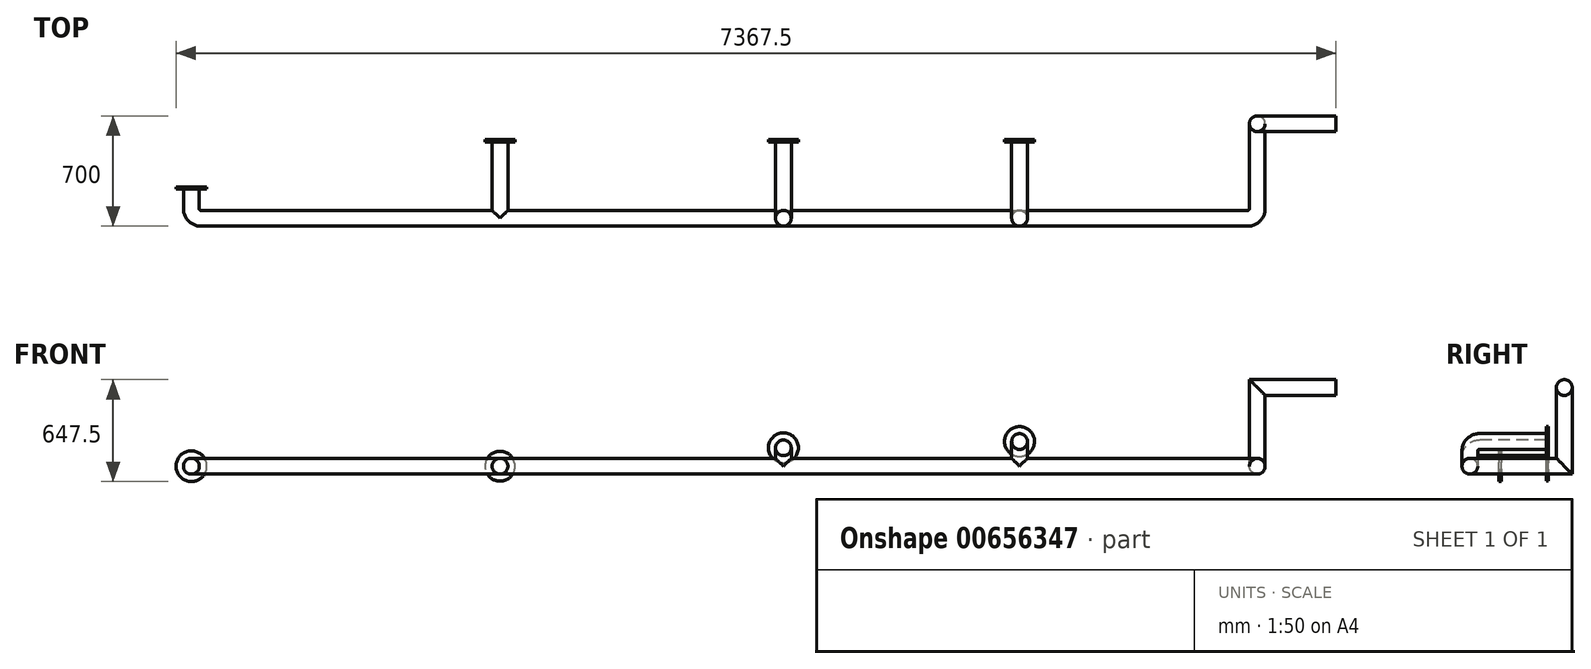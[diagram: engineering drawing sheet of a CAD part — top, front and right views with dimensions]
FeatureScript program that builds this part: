
annotation { "Feature Type Name" : "Feature", "Feature Type Description" : "" }
export const myFeature = defineFeature(function(context is Context, id is Id, definition is map)
    precondition{}
    {
        {
            var Q0;
            Q0=qCreatedBy(makeId("Top.planeOp"),FACE);
            var sketch = newSketch(context, id + "F0", { "sketchPlane" : qUnion([Q0])});
            skLineSegment(sketch, "E0", {"start": v(60, 0) * mm, "end": v(6710, 0) * mm});
            skLineSegment(sketch, "E1", {"start": v(6770, 60) * mm, "end": v(6770, 540) * mm});
            skLineSegment(sketch, "E2", {"start": v(0, 60) * mm, "end": v(0, 200) * mm});
            skLineSegment(sketch, "E3", {"start": v(1960.38, 0) * mm, "end": v(1960.38, 500) * mm});
            skLineSegment(sketch, "E4", {"start": v(3760, 0) * mm, "end": v(3760, 500) * mm});
            skLineSegment(sketch, "E5", {"start": v(5260, 0) * mm, "end": v(5260, 500) * mm});
            skPoint(sketch, "E6.visualSharp", {"position": v(0, 0) * mm});
            skArc(sketch, "E6.filletArc", {"start": v(0, 60) * mm, "mid": v(17.57, 17.57) * mm, "end": v(60, 0) * mm});
            skPoint(sketch, "E7.visualSharp", {"position": v(6770, 0) * mm});
            skArc(sketch, "E7.filletArc", {"start": v(6710, 0) * mm, "mid": v(6752.43, 17.57) * mm, "end": v(6770, 60) * mm});
            skPoint(sketch, "E8.visualSharp", {"position": v(6770, 600) * mm});
            skLineSegment(sketch, "E9", {"start": v(6770, 600) * mm, "end": v(6770, 540) * mm});
            skSolve(sketch);
        }
        {
            var Q0;
            Q0=qCreatedBy(makeId("Front.planeOp"),FACE);
            cPlane(context, id + "F1", {"entities" : qUnion([Q0]), "cplaneType" : CPlaneType.OFFSET, "offset" : 200 * mm, "oppositeDirection" : true, "width" : 150 * mm, "height" : 150 * mm});
        }
        {
            var Q0;
            Q0=qCreatedBy(id+"F1.planeOp",FACE);
            var sketch = newSketch(context, id + "F2", { "sketchPlane" : qUnion([Q0])});
            skCircle(sketch, "E10", {"center": v(0, 0) * mm, "radius": 97.5 * mm});
            skCircle(sketch, "E11", {"center": v(0, 0) * mm, "radius": 50 * mm});
            skSolve(sketch);
        }
        {
            var Q0;
            Q0=qCreatedBy(makeId("Front.planeOp"),FACE);
            cPlane(context, id + "F3", {"entities" : qUnion([Q0]), "cplaneType" : CPlaneType.OFFSET, "offset" : 500 * mm, "oppositeDirection" : true, "width" : 150 * mm, "height" : 150 * mm});
        }
        {
            var Q0;
            Q0=qCreatedBy(makeId("Right.planeOp"),FACE);
            cPlane(context, id + "F4", {"entities" : qUnion([Q0]), "cplaneType" : CPlaneType.OFFSET, "offset" : 6770 * mm, "width" : 150 * mm, "height" : 150 * mm});
        }
        {
            var Q0;
            Q0=qCreatedBy(id+"F4.planeOp",FACE);
            var sketch = newSketch(context, id + "F5", { "sketchPlane" : qUnion([Q0])});
            skPoint(sketch, "E12.0", {"position": v(600, 0) * mm});
            skLineSegment(sketch, "E13", {"start": v(600, 0) * mm, "end": v(600, 500) * mm});
            skSolve(sketch);
        }
        {
            var Q0;
            Q0=qCreatedBy(makeId("Front.planeOp"),FACE);
            cPlane(context, id + "F6", {"entities" : qUnion([Q0]), "cplaneType" : CPlaneType.OFFSET, "offset" : 600 * mm, "oppositeDirection" : true, "width" : 150 * mm, "height" : 150 * mm});
        }
        {
            var Q0;
            Q0=qCreatedBy(id+"F6.planeOp",FACE);
            var sketch = newSketch(context, id + "F7", { "sketchPlane" : qUnion([Q0])});
            skPoint(sketch, "E14.0", {"position": v(6770, 500) * mm});
            skLineSegment(sketch, "E15", {"start": v(6770, 500) * mm, "end": v(7270, 500) * mm});
            skSolve(sketch);
        }
        {
            var Q0;
            Q0=makeQuery(id+"F2.imprint","IMPRINT",FACE,{"disambiguationData":[TD([[makeQuery(id+"F2.imprint","IMPRINT",EDGE,{"derivedFrom":sQuery(id+"F2.wireOp",EDGE,"E11")}),1.0]])]});
            var Q1;
            Q1=sQuery(id+"F0.wireOp",EDGE,"E2");
            var Q2;
            Q2=sQuery(id+"F0.wireOp",EDGE,"E6.filletArc");
            var Q3;
            Q3=sQuery(id+"F0.wireOp",EDGE,"E0");
            var Q4;
            Q4=sQuery(id+"F0.wireOp",EDGE,"E7.filletArc");
            var Q5;
            Q5=sQuery(id+"F0.wireOp",EDGE,"E1");
            var Q6;
            Q6=sQuery(id+"F0.wireOp",EDGE,"E9");
            var Q7;
            Q7=sQuery(id+"F5.wireOp",EDGE,"E13");
            var Q8;
            Q8=sQuery(id+"F7.wireOp",EDGE,"E15");
            sweep(context, id + "F8", {"profiles" : qUnion([Q0]), "path" : qUnion([Q1, Q2, Q3, Q4, Q5, Q6, Q7, Q8])});
        }
        {
            var Q0;
            Q0=makeQuery(id+"F2.imprint","IMPRINT",FACE,{"disambiguationData":[TD([[makeQuery(id+"F2.imprint","IMPRINT",EDGE,{"derivedFrom":sQuery(id+"F2.wireOp",EDGE,"E10")}),1.0]])]});
            var Q1;
            Q1=makeQuery(id+"F2.imprint","IMPRINT",FACE,{"disambiguationData":[TD([[makeQuery(id+"F2.imprint","IMPRINT",EDGE,{"derivedFrom":sQuery(id+"F2.wireOp",EDGE,"E11")}),1.0]])]});
            var Q2;
            Q2=makeQuery(id+"F14.imprint","IMPRINT",FACE,{"disambiguationData":[TD([[makeQuery(id+"F14.imprint","IMPRINT",EDGE,{"derivedFrom":sQuery(id+"F14.wireOp",EDGE,"E27")}),1.0]])]});
            var Q3;
            Q3=makeQuery(id+"F14.imprint","IMPRINT",FACE,{"disambiguationData":[TD([[makeQuery(id+"F14.imprint","IMPRINT",EDGE,{"derivedFrom":sQuery(id+"F14.wireOp",EDGE,"E27")}),-1.0]])]});
            var Q4;
            Q4=makeQuery(id+"F14.imprint","IMPRINT",FACE,{"disambiguationData":[TD([[makeQuery(id+"F14.imprint","IMPRINT",EDGE,{"derivedFrom":sQuery(id+"F14.wireOp",EDGE,"sqqdmA6Q-mzdJ-ofS7-DpPN-aGv7wqR64nl4")}),1.0]])]});
            var Q5;
            Q5=makeQuery(id+"F14.imprint","IMPRINT",FACE,{"disambiguationData":[TD([[makeQuery(id+"F14.imprint","IMPRINT",EDGE,{"derivedFrom":sQuery(id+"F14.wireOp",EDGE,"sqqdmA6Q-mzdJ-ofS7-DpPN-aGv7wqR64nl4")}),-1.0]])]});
            var Q6;
            Q6=makeQuery(id+"F14.imprint","IMPRINT",FACE,{"disambiguationData":[TD([[makeQuery(id+"F14.imprint","IMPRINT",EDGE,{"derivedFrom":sQuery(id+"F14.wireOp",EDGE,"EQ2HYSVV-SNuf-yqh0-8dQJ-ssxWtkKtriHU")}),1.0]])]});
            var Q7;
            Q7=makeQuery(id+"F14.imprint","IMPRINT",FACE,{"disambiguationData":[TD([[makeQuery(id+"F14.imprint","IMPRINT",EDGE,{"derivedFrom":sQuery(id+"F14.wireOp",EDGE,"EQ2HYSVV-SNuf-yqh0-8dQJ-ssxWtkKtriHU")}),-1.0]])]});
            extrude(context, id + "F9", {"entities" : qUnion([Q0, Q1, Q2, Q3, Q4, Q5, Q6, Q7]), "operationType" : NewBodyOperationType.ADD, "depth" : 15 * mm, "offsetDistance" : 25 * mm});
        }
        {
            var Q0;
            Q0=qCreatedBy(makeId("Right.planeOp"),FACE);
            cPlane(context, id + "F10", {"entities" : qUnion([Q0]), "cplaneType" : CPlaneType.OFFSET, "offset" : 3760 * mm, "width" : 150 * mm, "height" : 150 * mm});
        }
        {
            var Q0;
            Q0=qCreatedBy(id+"F10.planeOp",FACE);
            var sketch = newSketch(context, id + "F11", { "sketchPlane" : qUnion([Q0])});
            skPoint(sketch, "E16.0", {"position": v(0, 0) * mm});
            skLineSegment(sketch, "E17", {"start": v(0, 0) * mm, "end": v(0, 57) * mm});
            skLineSegment(sketch, "E18", {"start": v(60, 117) * mm, "end": v(500, 117) * mm});
            skPoint(sketch, "E19.visualSharp", {"position": v(0, 117) * mm});
            skArc(sketch, "E19.filletArc", {"start": v(60, 117) * mm, "mid": v(17.57, 99.43) * mm, "end": v(0, 57) * mm});
            skSolve(sketch);
        }
        {
            var Q0;
            Q0=qCreatedBy(makeId("Right.planeOp"),FACE);
            cPlane(context, id + "F12", {"entities" : qUnion([Q0]), "cplaneType" : CPlaneType.OFFSET, "offset" : 5260 * mm, "width" : 150 * mm, "height" : 150 * mm});
        }
        {
            var Q0;
            Q0=qCreatedBy(id+"F12.planeOp",FACE);
            var sketch = newSketch(context, id + "F13", { "sketchPlane" : qUnion([Q0])});
            skPoint(sketch, "E20.0", {"position": v(0, 0) * mm});
            skLineSegment(sketch, "E21", {"start": v(0, 0) * mm, "end": v(0, 97) * mm});
            skLineSegment(sketch, "E22", {"start": v(60, 157) * mm, "end": v(500, 157) * mm});
            skPoint(sketch, "E23.visualSharp", {"position": v(0, 157) * mm});
            skArc(sketch, "E23.filletArc", {"start": v(60, 157) * mm, "mid": v(17.57, 139.43) * mm, "end": v(0, 97) * mm});
            skSolve(sketch);
        }
        {
            var Q0;
            Q0=qCreatedBy(id+"F3.planeOp",FACE);
            var sketch = newSketch(context, id + "F14", { "sketchPlane" : qUnion([Q0])});
            skPoint(sketch, "E24.0", {"position": v(1960.38, 0) * mm});
            skPoint(sketch, "E25.0", {"position": v(3760, 0) * mm});
            skPoint(sketch, "E26.0", {"position": v(5260, 0) * mm});
            skCircle(sketch, "E27", {"center": v(1960.38, 0) * mm, "radius": 50 * mm});
            skCircle(sketch, "E28", {"center": v(1960.38, 0) * mm, "radius": 95 * mm});
            skPoint(sketch, "E29.0", {"position": v(3760, 117) * mm});
            skCircle(sketch, "E30", {"center": v(3760, 117) * mm, "radius": 50 * mm});
            skCircle(sketch, "E31", {"center": v(3760, 117) * mm, "radius": 95 * mm});
            skPoint(sketch, "E32.0", {"position": v(5260, 157) * mm});
            skCircle(sketch, "E33", {"center": v(5260, 157) * mm, "radius": 50 * mm});
            skCircle(sketch, "E34", {"center": v(5260, 157) * mm, "radius": 95 * mm});
            skSolve(sketch);
        }
        {
            var Q0;
            Q0=makeQuery(id+"F14.imprint","IMPRINT",FACE,{"disambiguationData":[TD([[makeQuery(id+"F14.imprint","IMPRINT",EDGE,{"derivedFrom":sQuery(id+"F14.wireOp",EDGE,"E27")}),1.0]])]});
            var Q1;
            Q1=sQuery(id+"F0.wireOp",EDGE,"E3");
            sweep(context, id + "F15", {"operationType" : NewBodyOperationType.ADD, "profiles" : qUnion([Q0]), "path" : qUnion([Q1])});
        }
        {
            var Q0;
            Q0=makeQuery(id+"F14.imprint","IMPRINT",FACE,{"disambiguationData":[TD([[makeQuery(id+"F14.imprint","IMPRINT",EDGE,{"derivedFrom":sQuery(id+"F14.wireOp",EDGE,"E30")}),1.0]])]});
            var Q1;
            Q1=sQuery(id+"F11.wireOp",EDGE,"E18");
            var Q2;
            Q2=sQuery(id+"F11.wireOp",EDGE,"E19.filletArc");
            var Q3;
            Q3=sQuery(id+"F11.wireOp",EDGE,"E17");
            sweep(context, id + "F16", {"operationType" : NewBodyOperationType.ADD, "profiles" : qUnion([Q0]), "path" : qUnion([Q1, Q2, Q3])});
        }
        {
            var Q0;
            Q0=makeQuery(id+"F14.imprint","IMPRINT",FACE,{"disambiguationData":[TD([[makeQuery(id+"F14.imprint","IMPRINT",EDGE,{"derivedFrom":sQuery(id+"F14.wireOp",EDGE,"E33")}),1.0]])]});
            var Q1;
            Q1=sQuery(id+"F13.wireOp",EDGE,"E22");
            var Q2;
            Q2=sQuery(id+"F13.wireOp",EDGE,"E23.filletArc");
            var Q3;
            Q3=sQuery(id+"F13.wireOp",EDGE,"E21");
            sweep(context, id + "F17", {"operationType" : NewBodyOperationType.ADD, "profiles" : qUnion([Q0]), "path" : qUnion([Q1, Q2, Q3])});
        }
        {
            var Q0;
            Q0=makeQuery(id+"F14.imprint","IMPRINT",FACE,{"disambiguationData":[TD([[makeQuery(id+"F14.imprint","IMPRINT",EDGE,{"derivedFrom":sQuery(id+"F14.wireOp",EDGE,"E27")}),-1.0]])]});
            var Q1;
            Q1=makeQuery(id+"F14.imprint","IMPRINT",FACE,{"disambiguationData":[TD([[makeQuery(id+"F14.imprint","IMPRINT",EDGE,{"derivedFrom":sQuery(id+"F14.wireOp",EDGE,"E27")}),1.0]])]});
            var Q2;
            Q2=makeQuery(id+"F14.imprint","IMPRINT",FACE,{"disambiguationData":[TD([[makeQuery(id+"F14.imprint","IMPRINT",EDGE,{"derivedFrom":sQuery(id+"F14.wireOp",EDGE,"E30")}),1.0]])]});
            var Q3;
            Q3=makeQuery(id+"F14.imprint","IMPRINT",FACE,{"disambiguationData":[TD([[makeQuery(id+"F14.imprint","IMPRINT",EDGE,{"derivedFrom":sQuery(id+"F14.wireOp",EDGE,"E30")}),-1.0]])]});
            var Q4;
            Q4=makeQuery(id+"F14.imprint","IMPRINT",FACE,{"disambiguationData":[TD([[makeQuery(id+"F14.imprint","IMPRINT",EDGE,{"derivedFrom":sQuery(id+"F14.wireOp",EDGE,"E33")}),1.0]])]});
            var Q5;
            Q5=makeQuery(id+"F14.imprint","IMPRINT",FACE,{"disambiguationData":[TD([[makeQuery(id+"F14.imprint","IMPRINT",EDGE,{"derivedFrom":sQuery(id+"F14.wireOp",EDGE,"E33")}),-1.0]])]});
            extrude(context, id + "F18", {"entities" : qUnion([Q0, Q1, Q2, Q3, Q4, Q5]), "operationType" : NewBodyOperationType.ADD, "depth" : 15 * mm, "offsetDistance" : 25 * mm});
        }
    });
